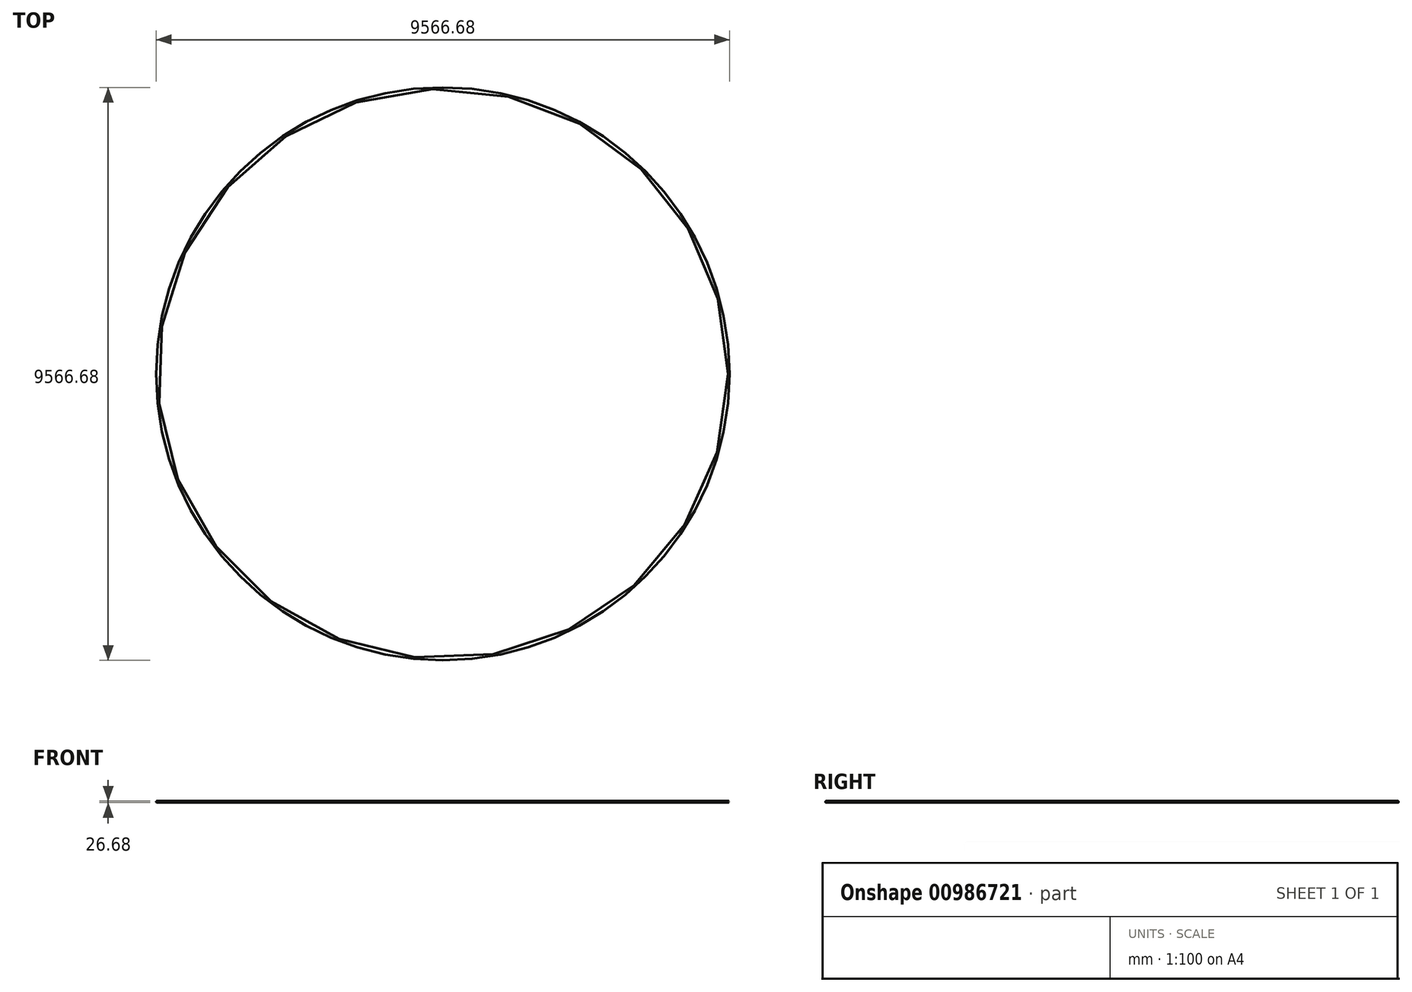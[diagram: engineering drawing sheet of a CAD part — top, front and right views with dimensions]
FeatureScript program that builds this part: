
annotation { "Feature Type Name" : "Feature", "Feature Type Description" : "" }
export const myFeature = defineFeature(function(context is Context, id is Id, definition is map)
    precondition{}
    {
        {
            var Q0;
            Q0=qCreatedBy(makeId("Front.planeOp"),FACE);
            var sketch = newSketch(context, id + "F0", { "sketchPlane" : qUnion([Q0])});
            skLineSegment(sketch, "E0", {"start": v(0, 0) * mm, "end": v(4770, 0) * mm, "construction": true});
            skLineSegment(sketch, "E1", {"start": v(4770, 0) * mm, "end": v(4770, -100) * mm, "construction": true});
            skPoint(sketch, "E2.middle", {"position": v(0, 0) * mm});
            skCircle(sketch, "E3", {"center": v(0, 0) * mm, "radius": 13.33 * mm});
            skCircle(sketch, "E4.0", {"center": v(0, 0) * mm, "radius": 11.23 * mm});
            skSolve(sketch);
        }
        {
            var Q0;
            Q0 = qSketchRegion(id + "F0", true);
            var Q1;
            Q1=sQuery(id+"F0.wireOp",EDGE,"E1");
            revolve(context, id + "F1", {"surfaceOperationType" : NewSurfaceOperationType.NEW, "entities" : qUnion([Q0]), "axis" : qUnion([Q1]), "revolveType" : RevolveType.FULL});
        }
    });
